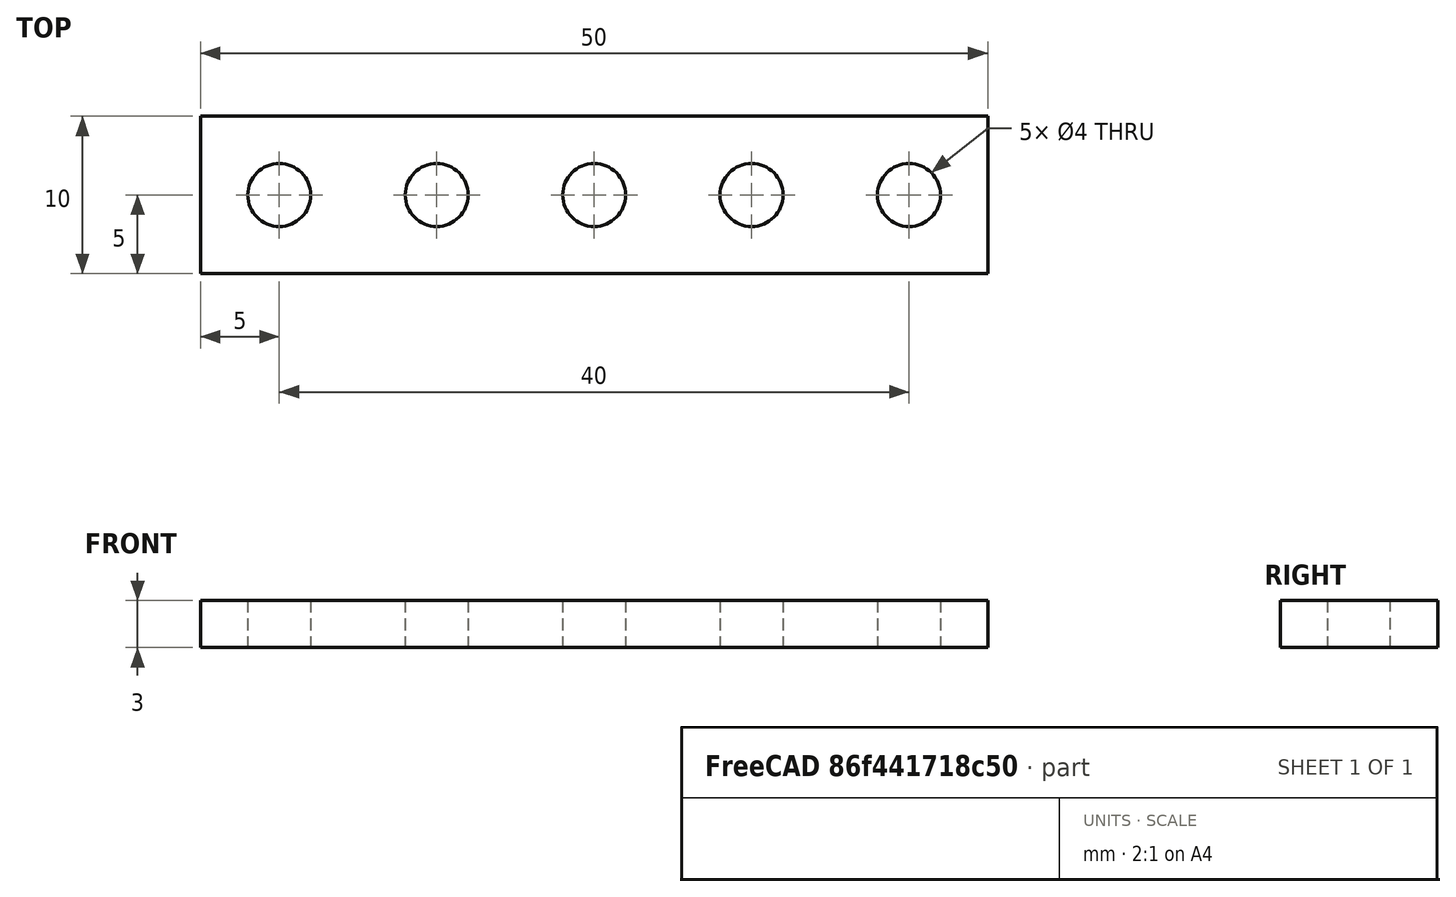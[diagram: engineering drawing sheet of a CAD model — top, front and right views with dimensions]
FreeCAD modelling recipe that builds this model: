
FCSTD DOCUMENT  (FreeCAD 0.20R29177 +233 (Git))
Label: mecano
License: All rights reserved
LicenseURL: http://en.wikipedia.org/wiki/All_rights_reserved
objects: Part::Cylinder×5, Part::Cut×5, Part::Box×1
note: 11 computed .brp shape members not serialized (recipe doc carries the construction recipe); baked Part::Feature solids carry a one-line shape summary decoded from their .brp

FEATURE [Part::Box] Box  label="Cubo"
  AttacherType = Attacher::AttachEngine3D
  Height = 3
  Length = 50
  Width = 10
FEATURE [Part::Cylinder] Cylinder001  label="Cilindro001"
  Angle = 360
  AttacherType = Attacher::AttachEngine3D
  FirstAngle = 0
  Height = 10
  Placement = pos=(45,5,0) rot=(0,0,1;1.5708rad)
  Radius = 2
  SecondAngle = 0
FEATURE [Part::Cylinder] Cylinder002  label="Cilindro002"
  Angle = 360
  AttacherType = Attacher::AttachEngine3D
  FirstAngle = 0
  Height = 10
  Placement = pos=(5,5,0) rot=(0,0,1;1.5708rad)
  Radius = 2
  SecondAngle = 0
FEATURE [Part::Cylinder] Cylinder003  label="Cilindro003"
  Angle = 360
  AttacherType = Attacher::AttachEngine3D
  FirstAngle = 0
  Height = 10
  Placement = pos=(15,5,0) rot=(0,0,1;1.5708rad)
  Radius = 2
  SecondAngle = 0
FEATURE [Part::Cylinder] Cylinder004  label="Cilindro004"
  Angle = 360
  AttacherType = Attacher::AttachEngine3D
  FirstAngle = 0
  Height = 10
  Placement = pos=(25,5,0) rot=(0,0,1;1.5708rad)
  Radius = 2
  SecondAngle = 0
FEATURE [Part::Cylinder] Cylinder005  label="Cilindro005"
  Angle = 360
  AttacherType = Attacher::AttachEngine3D
  FirstAngle = 0
  Height = 10
  Placement = pos=(35,5,0) rot=(0,0,1;1.5708rad)
  Radius = 2
  SecondAngle = 0
FEATURE [Part::Cut] Cut
  Base = -> Box
  Tool = -> Cylinder002
FEATURE [Part::Cut] Cut001
  Base = -> Cut
  Tool = -> Cylinder003
FEATURE [Part::Cut] Cut002
  Base = -> Cut001
  Tool = -> Cylinder004
FEATURE [Part::Cut] Cut003
  Base = -> Cut002
  Tool = -> Cylinder005
FEATURE [Part::Cut] Cut004
  Base = -> Cut003
  Tool = -> Cylinder001
